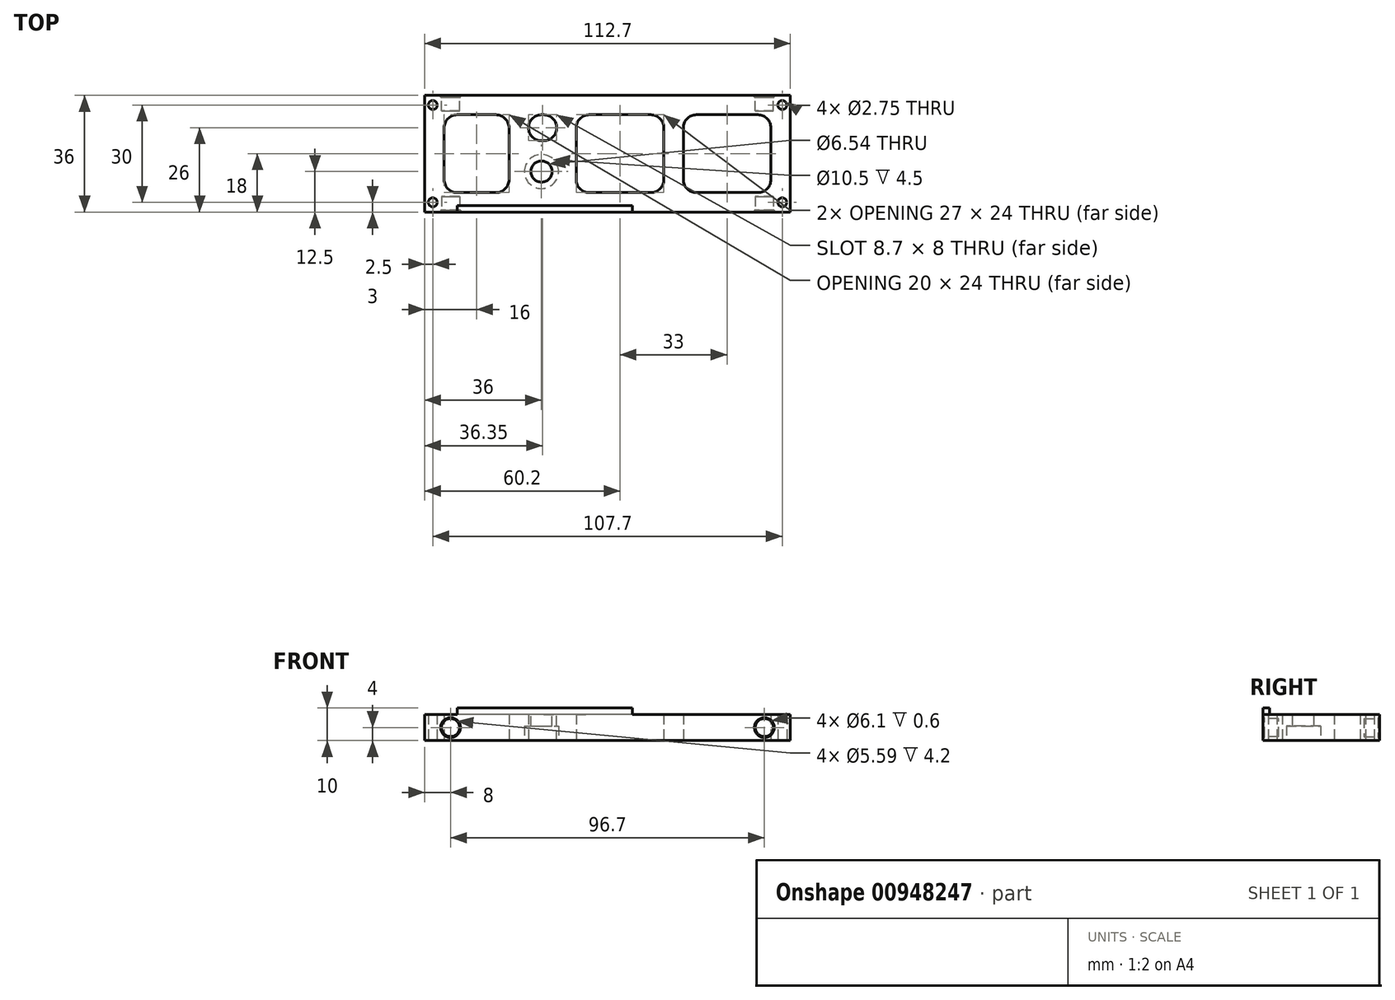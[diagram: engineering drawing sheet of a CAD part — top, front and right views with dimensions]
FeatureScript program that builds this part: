
annotation { "Feature Type Name" : "Feature", "Feature Type Description" : "" }
export const myFeature = defineFeature(function(context is Context, id is Id, definition is map)
    precondition{}
    {
        {
            var Q0;
            Q0=qCreatedBy(makeId("Top.planeOp"),FACE);
            var sketch = newSketch(context, id + "F0", { "sketchPlane" : qUnion([Q0])});
            skLineSegment(sketch, "E0.bottom", {"start": v(56.35, -18) * mm, "end": v(-56.35, -18) * mm});
            skLineSegment(sketch, "E0.top", {"start": v(56.35, 18) * mm, "end": v(-56.35, 18) * mm});
            skLineSegment(sketch, "E0.left", {"start": v(56.35, -18) * mm, "end": v(56.35, 18) * mm});
            skLineSegment(sketch, "E0.right", {"start": v(-56.35, -18) * mm, "end": v(-56.35, 18) * mm});
            skPoint(sketch, "E0.middle", {"position": v(0, 0) * mm});
            skSolve(sketch);
        }
        {
            var Q0;
            Q0=makeQuery(id+"F0.imprint","IMPRINT",FACE,{"disambiguationData":[TD([[makeQuery(id+"F0.imprint","IMPRINT",EDGE,{"derivedFrom":sQuery(id+"F0.wireOp",EDGE,"E0.bottom")}),-1.0]])]});
            extrude(context, id + "F1", {"entities" : qUnion([Q0]), "depth" : 8 * mm, "offsetDistance" : 25 * mm});
        }
        {
            var Q0;
            Q0=makeQuery(id+"F1.opExtrude","CAP_FACE",FACE,{"disambiguationData":[OSD([sQuery(id+"F0.wireOp",EDGE,"E0.bottom"),sQuery(id+"F0.wireOp",EDGE,"E0.top"),sQuery(id+"F0.wireOp",EDGE,"E0.left"),sQuery(id+"F0.wireOp",EDGE,"E0.right")])],"isStart":false});
            var sketch = newSketch(context, id + "F2", { "sketchPlane" : qUnion([Q0])});
            skSolve(sketch);
        }
        {
            var Q0;
            Q0=makeQuery(id+"F1.opExtrude","CAP_FACE",FACE,{"disambiguationData":[OSD([sQuery(id+"F0.wireOp",EDGE,"E0.bottom"),sQuery(id+"F0.wireOp",EDGE,"E0.top"),sQuery(id+"F0.wireOp",EDGE,"E0.left"),sQuery(id+"F0.wireOp",EDGE,"E0.right")])],"isStart":false});
            var sketch = newSketch(context, id + "F3", { "sketchPlane" : qUnion([Q0])});
            skLineSegment(sketch, "E1.bottom", {"start": v(7.65, -18) * mm, "end": v(-46.35, -18) * mm});
            skLineSegment(sketch, "E1.top", {"start": v(7.65, -16) * mm, "end": v(-46.35, -16) * mm});
            skLineSegment(sketch, "E1.left", {"start": v(7.65, -18) * mm, "end": v(7.65, -16) * mm});
            skLineSegment(sketch, "E1.right", {"start": v(-46.35, -18) * mm, "end": v(-46.35, -16) * mm});
            skSolve(sketch);
        }
        {
            var Q0;
            Q0=qSketchRegion(id+"F3",true);
            extrude(context, id + "F4", {"entities" : qUnion([Q0]), "operationType" : NewBodyOperationType.ADD, "depth" : 2 * mm, "offsetDistance" : 25 * mm});
        }
        {
            var Q0;
            Q0=makeQuery(id+"F2.imprint","IMPRINT",FACE,{"disambiguationData":[TD([[makeQuery(id+"F2.imprint","IMPRINT",EDGE,{"derivedFrom":makeQuery(id+"F1.opExtrude","CAP_EDGE",EDGE,{"disambiguationData":[OSD([sQuery(id+"F0.wireOp",EDGE,"E0.bottom")])],"isStart":false})}),-1.0]])]});
            var sketch = newSketch(context, id + "F5", { "sketchPlane" : qUnion([Q0])});
            skCircle(sketch, "E2", {"center": v(-20.35, -5.5) * mm, "radius": 3.27 * mm});
            skLineSegment(sketch, "E3", {"start": v(-45.06, -5.5) * mm, "end": v(5.93, -5.5) * mm, "construction": true});
            skLineSegment(sketch, "E4", {"start": v(-20.35, -15.31) * mm, "end": v(-20.35, 10.3) * mm, "construction": true});
            skSolve(sketch);
        }
        {
            var Q0;
            Q0=qSketchRegion(id+"F5",true);
            extrude(context, id + "F6", {"entities" : qUnion([Q0]), "operationType" : NewBodyOperationType.REMOVE, "endBound" : BoundingType.THROUGH_ALL, "oppositeDirection" : true, "depth" : 25 * mm, "offsetDistance" : 25 * mm});
        }
        {
            var Q0;
            Q0=makeQuery(id+"F1.opExtrude","CAP_FACE",FACE,{"disambiguationData":[OSD([sQuery(id+"F0.wireOp",EDGE,"E0.bottom"),sQuery(id+"F0.wireOp",EDGE,"E0.top"),sQuery(id+"F0.wireOp",EDGE,"E0.left"),sQuery(id+"F0.wireOp",EDGE,"E0.right")])],"isStart":true});
            var sketch = newSketch(context, id + "F7", { "sketchPlane" : qUnion([Q0])});
            skLineSegment(sketch, "E5", {"start": v(-65.19, 0) * mm, "end": v(58.26, 0) * mm, "construction": true});
            skLineSegment(sketch, "E6", {"start": v(0, 29.35) * mm, "end": v(0, -25.17) * mm, "construction": true});
            skPoint(sketch, "E6.endSnap0", {"position": v(0, -18) * mm});
            skCircle(sketch, "E7", {"center": v(-53.85, 15) * mm, "radius": 1.38 * mm});
            skCircle(sketch, "E8.0.1.0", {"center": v(-53.85, -15) * mm, "radius": 1.38 * mm});
            skCircle(sketch, "E8.1.0.0", {"center": v(53.85, 15) * mm, "radius": 1.38 * mm});
            skCircle(sketch, "E8.1.1.0", {"center": v(53.85, -15) * mm, "radius": 1.38 * mm});
            skLineSegment(sketch, "E8.direction1", {"start": v(-53.85, 15) * mm, "end": v(53.85, 15) * mm, "construction": true});
            skLineSegment(sketch, "E8.direction2", {"start": v(-53.85, 15) * mm, "end": v(-53.85, -15) * mm, "construction": true});
            skSolve(sketch);
        }
        {
            var Q0;
            Q0=makeQuery(id+"F7.imprint","IMPRINT",FACE,{"disambiguationData":[TD([[makeQuery(id+"F7.imprint","IMPRINT",EDGE,{"derivedFrom":sQuery(id+"F7.wireOp",EDGE,"E7")}),1.0]])]});
            var Q1;
            Q1=makeQuery(id+"F7.imprint","IMPRINT",FACE,{"disambiguationData":[TD([[makeQuery(id+"F7.imprint","IMPRINT",EDGE,{"derivedFrom":sQuery(id+"F7.wireOp",EDGE,"E8.0.1.0")}),1.0]])]});
            var Q2;
            Q2=makeQuery(id+"F7.imprint","IMPRINT",FACE,{"disambiguationData":[TD([[makeQuery(id+"F7.imprint","IMPRINT",EDGE,{"derivedFrom":sQuery(id+"F7.wireOp",EDGE,"E8.1.0.0")}),1.0]])]});
            var Q3;
            Q3=makeQuery(id+"F7.imprint","IMPRINT",FACE,{"disambiguationData":[TD([[makeQuery(id+"F7.imprint","IMPRINT",EDGE,{"derivedFrom":sQuery(id+"F7.wireOp",EDGE,"E8.1.1.0")}),1.0]])]});
            extrude(context, id + "F8", {"entities" : qUnion([Q0, Q1, Q2, Q3]), "operationType" : NewBodyOperationType.REMOVE, "endBound" : BoundingType.THROUGH_ALL, "oppositeDirection" : true, "depth" : 5.5 * mm, "offsetDistance" : 25 * mm});
        }
        {
            var Q0;
            Q0=makeQuery(id+"F1.opExtrude","CAP_FACE",FACE,{"disambiguationData":[OSD([sQuery(id+"F0.wireOp",EDGE,"E0.bottom"),sQuery(id+"F0.wireOp",EDGE,"E0.top"),sQuery(id+"F0.wireOp",EDGE,"E0.left"),sQuery(id+"F0.wireOp",EDGE,"E0.right")])],"isStart":true});
            var sketch = newSketch(context, id + "F9", { "sketchPlane" : qUnion([Q0])});
            skLineSegment(sketch, "E9.bottom", {"start": v(-50.35, 12) * mm, "end": v(-30.35, 12) * mm});
            skLineSegment(sketch, "E9.top", {"start": v(-50.35, -12) * mm, "end": v(-30.35, -12) * mm});
            skLineSegment(sketch, "E9.left", {"start": v(-50.35, 12) * mm, "end": v(-50.35, -12) * mm});
            skLineSegment(sketch, "E9.right", {"start": v(-30.35, 12) * mm, "end": v(-30.35, -12) * mm});
            skLineSegment(sketch, "E10.bottom", {"start": v(-9.65, 12) * mm, "end": v(17.35, 12) * mm});
            skLineSegment(sketch, "E10.top", {"start": v(-9.65, -12) * mm, "end": v(17.35, -12) * mm});
            skLineSegment(sketch, "E10.left", {"start": v(-9.65, 12) * mm, "end": v(-9.65, -12) * mm});
            skLineSegment(sketch, "E10.right", {"start": v(17.35, 12) * mm, "end": v(17.35, -12) * mm});
            skLineSegment(sketch, "E11.bottom", {"start": v(23.35, 12) * mm, "end": v(50.35, 12) * mm});
            skLineSegment(sketch, "E11.top", {"start": v(23.35, -12) * mm, "end": v(50.35, -12) * mm});
            skLineSegment(sketch, "E11.left", {"start": v(23.35, 12) * mm, "end": v(23.35, -12) * mm});
            skLineSegment(sketch, "E11.right", {"start": v(50.35, 12) * mm, "end": v(50.35, -12) * mm});
            skLineSegment(sketch, "E12.bottom", {"start": v(-24.35, -4) * mm, "end": v(-15.65, -4) * mm});
            skLineSegment(sketch, "E12.top", {"start": v(-24.35, -12) * mm, "end": v(-15.65, -12) * mm});
            skLineSegment(sketch, "E12.left", {"start": v(-24.35, -4) * mm, "end": v(-24.35, -12) * mm});
            skLineSegment(sketch, "E12.right", {"start": v(-15.65, -4) * mm, "end": v(-15.65, -12) * mm});
            skSolve(sketch);
        }
        {
            var Q0;
            Q0=makeQuery(id+"F9.imprint","IMPRINT",FACE,{"disambiguationData":[TD([[makeQuery(id+"F9.imprint","IMPRINT",EDGE,{"derivedFrom":sQuery(id+"F9.wireOp",EDGE,"E9.bottom")}),1.0]])]});
            var sketch = newSketch(context, id + "F10", { "sketchPlane" : qUnion([Q0])});
            skCircle(sketch, "E13", {"center": v(-20.35, 5.5) * mm, "radius": 5.25 * mm});
            skSolve(sketch);
        }
        {
            var Q0;
            Q0=qSketchRegion(id+"F10",true);
            extrude(context, id + "F11", {"entities" : qUnion([Q0]), "operationType" : NewBodyOperationType.REMOVE, "oppositeDirection" : true, "depth" : 4.5 * mm, "offsetDistance" : 25 * mm});
        }
        {
            var Q0;
            Q0=qSketchRegion(id+"F9",true);
            extrude(context, id + "F12", {"entities" : qUnion([Q0]), "operationType" : NewBodyOperationType.REMOVE, "endBound" : BoundingType.THROUGH_ALL, "oppositeDirection" : true, "depth" : 25 * mm, "offsetDistance" : 25 * mm});
        }
        {
            var Q0;
            Q0=makeQuery(id+"F12.boolean.opBoolean","COPY",EDGE,{"derivedFrom":makeQuery(id+"F12.opExtrude","SWEPT_EDGE",EDGE,{"disambiguationData":[OSD([sQuery(id+"F9.wireOp",EDGE,"E9.bottom"),sQuery(id+"F9.wireOp",EDGE,"E9.right")])]})});
            var Q1;
            Q1=makeQuery(id+"F12.boolean.opBoolean","COPY",EDGE,{"derivedFrom":makeQuery(id+"F12.opExtrude","SWEPT_EDGE",EDGE,{"disambiguationData":[OSD([sQuery(id+"F9.wireOp",EDGE,"E9.bottom"),sQuery(id+"F9.wireOp",EDGE,"E9.left")])]})});
            var Q2;
            Q2=makeQuery(id+"F12.boolean.opBoolean","COPY",EDGE,{"derivedFrom":makeQuery(id+"F12.opExtrude","SWEPT_EDGE",EDGE,{"disambiguationData":[OSD([sQuery(id+"F9.wireOp",EDGE,"E9.top"),sQuery(id+"F9.wireOp",EDGE,"E9.left")])]})});
            var Q3;
            Q3=makeQuery(id+"F12.boolean.opBoolean","COPY",EDGE,{"derivedFrom":makeQuery(id+"F12.opExtrude","SWEPT_EDGE",EDGE,{"disambiguationData":[OSD([sQuery(id+"F9.wireOp",EDGE,"E9.top"),sQuery(id+"F9.wireOp",EDGE,"E9.right")])]})});
            var Q4;
            Q4=makeQuery(id+"F12.boolean.opBoolean","COPY",EDGE,{"derivedFrom":makeQuery(id+"F12.opExtrude","SWEPT_EDGE",EDGE,{"disambiguationData":[OSD([sQuery(id+"F9.wireOp",EDGE,"E12.bottom"),sQuery(id+"F9.wireOp",EDGE,"E12.left")])]})});
            var Q5;
            Q5=makeQuery(id+"F12.boolean.opBoolean","COPY",EDGE,{"derivedFrom":makeQuery(id+"F12.opExtrude","SWEPT_EDGE",EDGE,{"disambiguationData":[OSD([sQuery(id+"F9.wireOp",EDGE,"E10.bottom"),sQuery(id+"F9.wireOp",EDGE,"E10.left")])]})});
            var Q6;
            Q6=makeQuery(id+"F12.boolean.opBoolean","COPY",EDGE,{"derivedFrom":makeQuery(id+"F12.opExtrude","SWEPT_EDGE",EDGE,{"disambiguationData":[OSD([sQuery(id+"F9.wireOp",EDGE,"E11.bottom"),sQuery(id+"F9.wireOp",EDGE,"E11.left")])]})});
            var Q7;
            Q7=makeQuery(id+"F12.boolean.opBoolean","COPY",EDGE,{"derivedFrom":makeQuery(id+"F12.opExtrude","SWEPT_EDGE",EDGE,{"disambiguationData":[OSD([sQuery(id+"F9.wireOp",EDGE,"E10.top"),sQuery(id+"F9.wireOp",EDGE,"E10.left")])]})});
            var Q8;
            Q8=makeQuery(id+"F12.boolean.opBoolean","COPY",EDGE,{"derivedFrom":makeQuery(id+"F12.opExtrude","SWEPT_EDGE",EDGE,{"disambiguationData":[OSD([sQuery(id+"F9.wireOp",EDGE,"E12.top"),sQuery(id+"F9.wireOp",EDGE,"E12.left")])]})});
            var Q9;
            Q9=makeQuery(id+"F12.boolean.opBoolean","COPY",EDGE,{"derivedFrom":makeQuery(id+"F12.opExtrude","SWEPT_EDGE",EDGE,{"disambiguationData":[OSD([sQuery(id+"F9.wireOp",EDGE,"E10.bottom"),sQuery(id+"F9.wireOp",EDGE,"E10.right")])]})});
            var Q10;
            Q10=makeQuery(id+"F12.boolean.opBoolean","COPY",EDGE,{"derivedFrom":makeQuery(id+"F12.opExtrude","SWEPT_EDGE",EDGE,{"disambiguationData":[OSD([sQuery(id+"F9.wireOp",EDGE,"E11.bottom"),sQuery(id+"F9.wireOp",EDGE,"E11.right")])]})});
            var Q11;
            Q11=makeQuery(id+"F12.boolean.opBoolean","COPY",EDGE,{"derivedFrom":makeQuery(id+"F12.opExtrude","SWEPT_EDGE",EDGE,{"disambiguationData":[OSD([sQuery(id+"F9.wireOp",EDGE,"E11.top"),sQuery(id+"F9.wireOp",EDGE,"E11.right")])]})});
            var Q12;
            Q12=makeQuery(id+"F12.boolean.opBoolean","COPY",EDGE,{"derivedFrom":makeQuery(id+"F12.opExtrude","SWEPT_EDGE",EDGE,{"disambiguationData":[OSD([sQuery(id+"F9.wireOp",EDGE,"E11.top"),sQuery(id+"F9.wireOp",EDGE,"E11.left")])]})});
            var Q13;
            Q13=makeQuery(id+"F12.boolean.opBoolean","COPY",EDGE,{"derivedFrom":makeQuery(id+"F12.opExtrude","SWEPT_EDGE",EDGE,{"disambiguationData":[OSD([sQuery(id+"F9.wireOp",EDGE,"E12.bottom"),sQuery(id+"F9.wireOp",EDGE,"E12.right")])]})});
            var Q14;
            Q14=makeQuery(id+"F12.boolean.opBoolean","COPY",EDGE,{"derivedFrom":makeQuery(id+"F12.opExtrude","SWEPT_EDGE",EDGE,{"disambiguationData":[OSD([sQuery(id+"F9.wireOp",EDGE,"E12.top"),sQuery(id+"F9.wireOp",EDGE,"E12.right")])]})});
            var Q15;
            Q15=makeQuery(id+"F12.boolean.opBoolean","COPY",EDGE,{"derivedFrom":makeQuery(id+"F12.opExtrude","SWEPT_EDGE",EDGE,{"disambiguationData":[OSD([sQuery(id+"F9.wireOp",EDGE,"E10.top"),sQuery(id+"F9.wireOp",EDGE,"E10.right")])]})});
            fillet(context, id + "F13", {"entities" : qUnion([Q0, Q1, Q2, Q3, Q4, Q5, Q6, Q7, Q8, Q9, Q10, Q11, Q12, Q13, Q14, Q15]), "radius" : 4 * mm, "tangentPropagation" : true, "allowEdgeOverflow" : false});
        }
        {
            var Q0;
            Q0=makeQuery(id+"F4.boolean.opBoolean","MERGE",FACE,{"derivedFrom":[makeQuery(id+"F1.opExtrude","SWEPT_FACE",FACE,{"disambiguationData":[OSD([sQuery(id+"F0.wireOp",EDGE,"E0.bottom")])]}),makeQuery(id+"F4.opExtrude","SWEPT_FACE",FACE,{"disambiguationData":[OSD([sQuery(id+"F3.wireOp",EDGE,"E1.bottom")])]})]});
            var sketch = newSketch(context, id + "F14", { "sketchPlane" : qUnion([Q0])});
            skCircle(sketch, "E14", {"center": v(-48.35, 4) * mm, "radius": 2.8 * mm});
            skPoint(sketch, "E14.centerSnap0", {"position": v(-56.35, 4) * mm});
            skCircle(sketch, "E15", {"center": v(48.35, 4) * mm, "radius": 2.8 * mm});
            skSolve(sketch);
        }
        {
            var Q0;
            Q0=makeQuery(id+"F14.imprint","IMPRINT",FACE,{"disambiguationData":[TD([[makeQuery(id+"F14.imprint","IMPRINT",EDGE,{"derivedFrom":sQuery(id+"F14.wireOp",EDGE,"E15")}),1.0]])]});
            var Q1;
            Q1=makeQuery(id+"F14.imprint","IMPRINT",FACE,{"disambiguationData":[TD([[makeQuery(id+"F14.imprint","IMPRINT",EDGE,{"derivedFrom":sQuery(id+"F14.wireOp",EDGE,"E14")}),1.0]])]});
            extrude(context, id + "F15", {"entities" : qUnion([Q0, Q1]), "operationType" : NewBodyOperationType.REMOVE, "oppositeDirection" : true, "depth" : 4.8 * mm, "offsetDistance" : 25 * mm});
        }
        {
            var Q0;
            Q0=makeQuery(id+"F1.opExtrude","SWEPT_FACE",FACE,{"disambiguationData":[OSD([sQuery(id+"F0.wireOp",EDGE,"E0.top")])]});
            var sketch = newSketch(context, id + "F16", { "sketchPlane" : qUnion([Q0])});
            skCircle(sketch, "E16", {"center": v(-48.35, 4) * mm, "radius": 2.8 * mm});
            skPoint(sketch, "E16.centerSnap0", {"position": v(-56.35, 4) * mm});
            skCircle(sketch, "E17", {"center": v(48.35, 4) * mm, "radius": 2.8 * mm});
            skPoint(sketch, "E17.centerSnap0", {"position": v(56.35, 4) * mm});
            skSolve(sketch);
        }
        {
            var Q0;
            Q0=makeQuery(id+"F16.imprint","IMPRINT",FACE,{"disambiguationData":[TD([[makeQuery(id+"F16.imprint","IMPRINT",EDGE,{"derivedFrom":sQuery(id+"F16.wireOp",EDGE,"E17")}),1.0]])]});
            var Q1;
            Q1=makeQuery(id+"F16.imprint","IMPRINT",FACE,{"disambiguationData":[TD([[makeQuery(id+"F16.imprint","IMPRINT",EDGE,{"derivedFrom":sQuery(id+"F16.wireOp",EDGE,"E16")}),1.0]])]});
            extrude(context, id + "F17", {"entities" : qUnion([Q0, Q1]), "operationType" : NewBodyOperationType.REMOVE, "oppositeDirection" : true, "depth" : 4.8 * mm, "offsetDistance" : 25 * mm});
        }
        {
            var Q0;
            Q0=makeQuery(id+"F4.boolean.opBoolean","MERGE",FACE,{"derivedFrom":[makeQuery(id+"F1.opExtrude","SWEPT_FACE",FACE,{"disambiguationData":[OSD([sQuery(id+"F0.wireOp",EDGE,"E0.bottom")])]}),makeQuery(id+"F4.opExtrude","SWEPT_FACE",FACE,{"disambiguationData":[OSD([sQuery(id+"F3.wireOp",EDGE,"E1.bottom")])]})]});
            var sketch = newSketch(context, id + "F18", { "sketchPlane" : qUnion([Q0])});
            skCircle(sketch, "E18", {"center": v(-48.35, 4) * mm, "radius": 3.05 * mm});
            skCircle(sketch, "E19", {"center": v(48.35, 4) * mm, "radius": 3.05 * mm});
            skSolve(sketch);
        }
        {
            var Q0;
            Q0 = qSketchRegion(id + "F18", true);
            extrude(context, id + "F19", {"entities" : qUnion([Q0]), "operationType" : NewBodyOperationType.REMOVE, "oppositeDirection" : true, "depth" : 0.6 * mm, "offsetDistance" : 25 * mm});
        }
        {
            var Q0;
            Q0=makeQuery(id+"F1.opExtrude","SWEPT_FACE",FACE,{"disambiguationData":[OSD([sQuery(id+"F0.wireOp",EDGE,"E0.top")])]});
            var sketch = newSketch(context, id + "F20", { "sketchPlane" : qUnion([Q0])});
            skCircle(sketch, "E20", {"center": v(-48.35, 4) * mm, "radius": 3.05 * mm});
            skCircle(sketch, "E21", {"center": v(48.35, 4) * mm, "radius": 3.05 * mm});
            skSolve(sketch);
        }
        {
            var Q0;
            Q0 = qSketchRegion(id + "F20", true);
            extrude(context, id + "F21", {"entities" : qUnion([Q0]), "operationType" : NewBodyOperationType.REMOVE, "oppositeDirection" : true, "depth" : 0.6 * mm, "offsetDistance" : 25 * mm});
        }
    });
